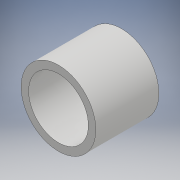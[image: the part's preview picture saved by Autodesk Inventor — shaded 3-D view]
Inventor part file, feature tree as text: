
AUTODESK INVENTOR PART (.ipt)
format: ipt  version: 2018 (Build 220112000, 112)  size: 218,624 bytes
history: native  units: mm
features: extrude x1, sketch x1
ambient origin geometry x8: Origin, YZ Plane, XZ Plane, XY Plane, X Axis, Y Axis, Z Axis, Center Point
bodies: Solid1 (feature_tree)
feature tree (2):
  extrude  "Extrusion1"  Depth=6.75mm
  sketch  "Sketch1"  dims[d0=6.4mm d1=8.0mm d2=6.75mm d3=0.0mm]
